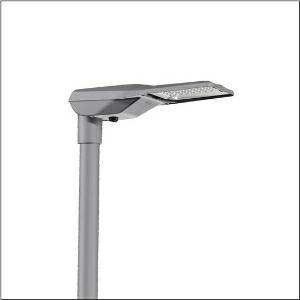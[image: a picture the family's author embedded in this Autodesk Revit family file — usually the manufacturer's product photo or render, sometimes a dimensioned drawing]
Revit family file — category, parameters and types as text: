
# Revit family: streetlight_sl_21_mini___p0_8ab_5xe2r33r08gb_1b3d
name_source: partatom
category: Lighting Fixtures
units: mm (PartAtom-declared; Revit-internal decimal feet)

## family parameters
Cut with Voids When Loaded = No
Host = Face
Light Source = No
Part Type = Normal
Room Calculation Point = No
Round Connector Dimension = Use Diameter
Shared = No

## types (1)
- --- (1 x LED, 5160 lm, 40.4 W, 3000K)
    Apparent Load = 40 VA
    CIE Flux Codes = 36 71 98 100 100
    Color Rendering = 70
    Color Temperature = 3000K
    Default Elevation = 1800 mm
    Description = Streetlight SL 21 mini, mast luminaire, primary light control with lens, of PMMA, primary optical cover: cover, of toughened safety glass, transparent, light distribution: P0.8aB, light emission: direct distribution, primary light characteristic: asymmetric, installation type: post-top, side-entry, LED, High Power LED, rated luminous flux: 5.160lm, luminous efficacy: 128lm/W, light colour: 730, colour temperature: 3000K, control gear: D4i, control: pre-setting: logarithmic dimming characteristic, flexible luminous flux parameterisation, time-dependent luminous flux control, constant luminous flux control, overheat protection, mains connection: 220..240V, AC, 50/60Hz, start of lifetime: 40W, end of service life: 41W, reduction: 19W, luminaire housing, of diecast aluminium, powder-coated, SITECO metallic grey (DB 702S), corrosivity category C5 high according to DIN EN ISO 12944, multi-level sealing system, sealing non-destructively replaceable, inclination adjustable: 0°, 5°, 10°, 15°, please order mast flange separately, length: 628mm, width: 235mm, height: 110mm, mast flange for spigot size: 42mm (side-entry): 5XC10008XM4, 60/48mm (side-entry/post-top): 5XC10108XM2, 76/60mm (side-entry/post-top): 5XC10108XM1, mounting height: 4..8m, Smart Interface below, protection rating (complete): IP66, insulation class (complete): insulation class II (safety insulation), certification: CE, ENEC, ENEC+, VDE, impact resistance: IK10, permissible operating ambient temperature for outdoor applications: -40..+50°C, standard-compliant lighting for roads and squares, packaging unit: 1 piece

Light Distribution: P0.8aB
    Height = 110 mm
    Lamp = 1 x LED
    Lamp Light Flux = 5160 lm
    Lamp Power = 40.4 W
    Lamp count = 1
    Length = 625 mm
    Luminous efficacy = 128 lm/W
    Manufacturer = Siteco
    ModVariant = No
    Model = 5XE2R33R08GB
    Number of Poles = 1
    OnlyDefault = Yes
    Power Factor = 1
    Product Name = Streetlight SL 21 mini | P0.8aB
    Product group = mast luminaire | pylon top
    ProductGroupID = 6100
    Protection Class = Protection class II
    Protection Degree = IP 66
    RLX_Detail_Level = 1
    RLX_Emergency_Light_Flux = 0 lm
    RLX_Emergency_Type = 0
    RLX_Emergency_Type_DB = No
    RlxData = <blob elided: 92101 chars, md5=58e5b062>
    Socket = socket
    Standby Power = 0 W
    System Light Flux = 5160 lm
    System Power = 40 W
    Type Comments = factory setting: luminous flux: 100 % | dim-lin: 254 | 812 mA
    Type Image = l_1003516.jpg
    URL = http://relux.com
    VarID = @adj_082415
    Voltage = 0 V
    Weight = 0.00 kg
    Width = 234 mm

## geometry (parser evidence)
native form markers: Blend x4, Sweep x11
no freeform markers — native parametric forms only
